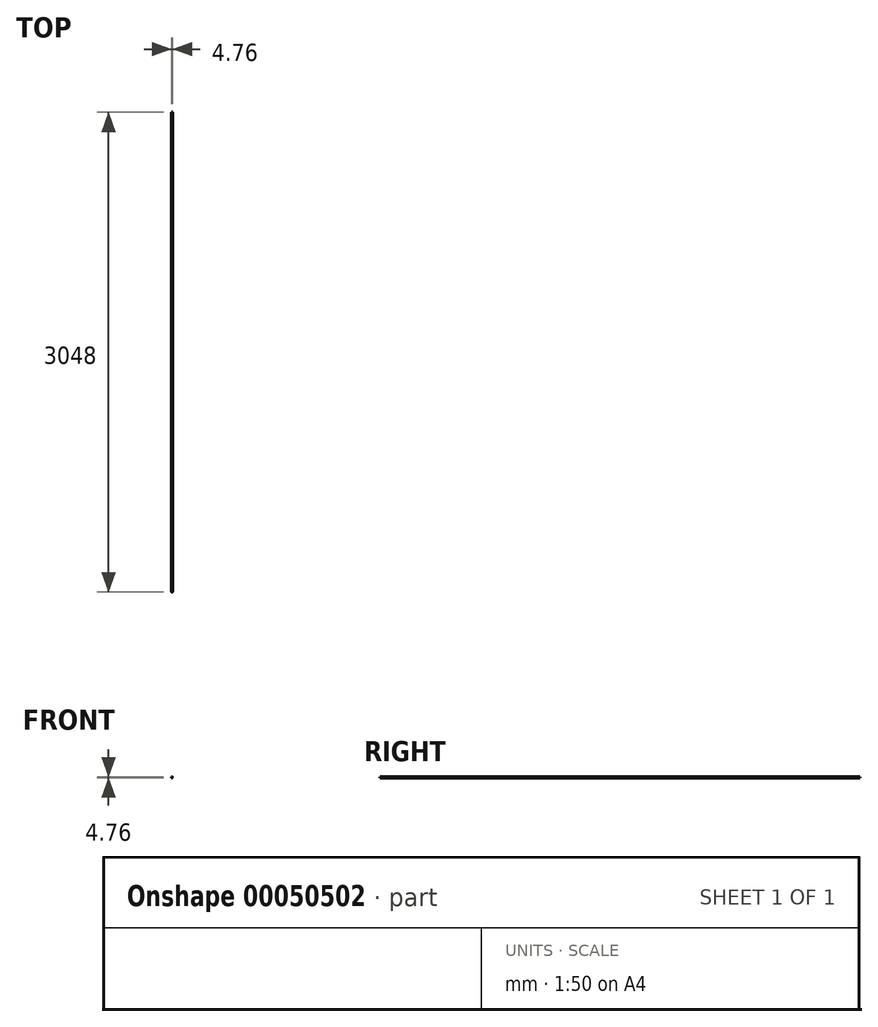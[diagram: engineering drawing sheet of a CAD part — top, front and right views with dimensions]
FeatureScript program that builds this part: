
annotation { "Feature Type Name" : "Feature", "Feature Type Description" : "" }
export const myFeature = defineFeature(function(context is Context, id is Id, definition is map)
    precondition{}
    {
        {
            var Q0;
            Q0=qCreatedBy(makeId("Front.planeOp"),FACE);
            var sketch = newSketch(context, id + "F0", { "sketchPlane" : qUnion([Q0])});
            skCircle(sketch, "E0", {"center": v(0, 0) * mm, "radius": 2.38 * mm});
            skSolve(sketch);
        }
        {
            var Q0;
            Q0=qSketchRegion(id+"F0",true);
            extrude(context, id + "F1", {"entities" : qUnion([Q0]), "endBound" : BoundingType.SYMMETRIC, "depth" : 3048 * mm});
        }
    });
